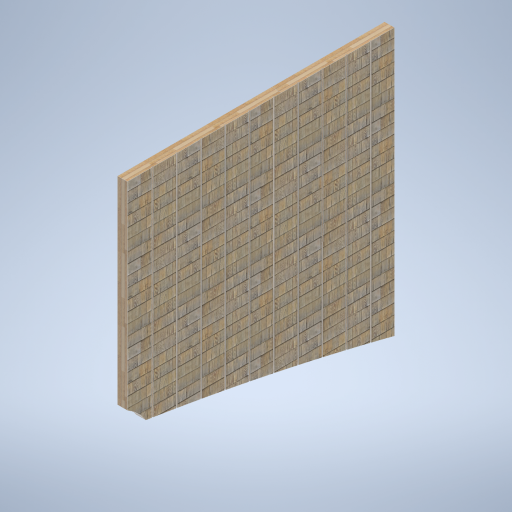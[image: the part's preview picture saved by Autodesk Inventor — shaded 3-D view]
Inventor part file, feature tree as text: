
AUTODESK INVENTOR PART (.ipt)
format: ipt  version: 2024.2 (Build 282272000, 272)  size: 504,320 bytes
history: native  units: in
note: dims shown in document units (in); Inventor stores cm internally (conversion verified against a paired STEP export)
features: other x3, sketch x2
ambient origin geometry x8: Origin, YZ Plane, XZ Plane, XY Plane, X Axis, Y Axis, Z Axis, Center Point
bodies: Solid1 (feature_tree)
feature tree (5):
  other  "side_wall_01_MIR.ipt"
  other  "Solid1::side_wall_01_MIR.ipt"
  other  "TaggingFeature1"
  sketch  "Sketch1"  dims[d0=0.3937in]
  sketch  "Sketch2"
